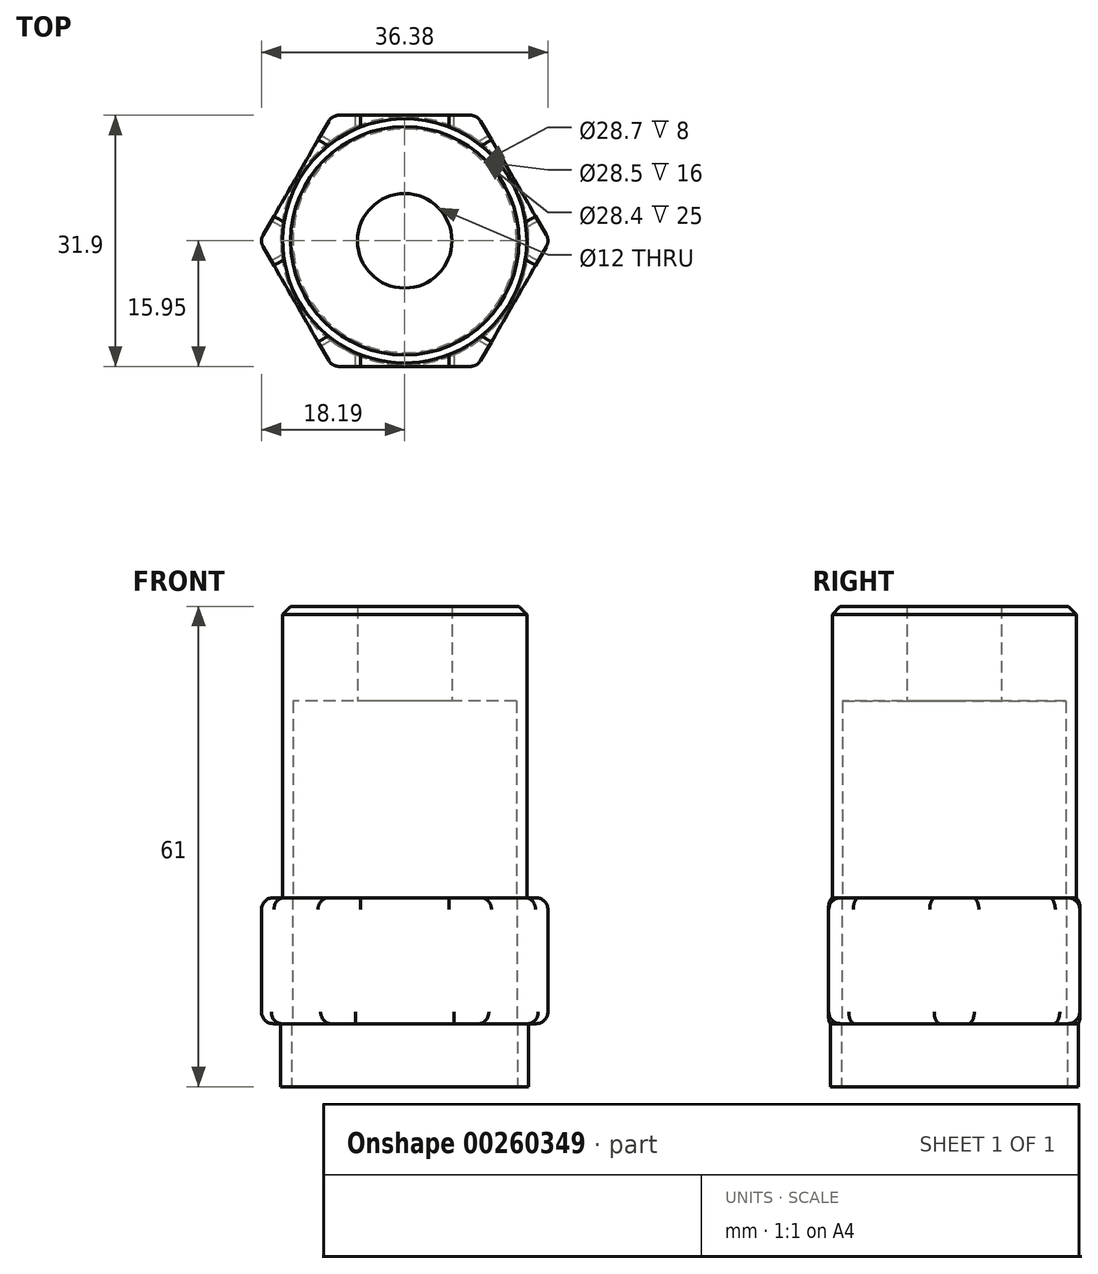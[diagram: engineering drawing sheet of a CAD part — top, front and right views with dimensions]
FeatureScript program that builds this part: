
annotation { "Feature Type Name" : "Feature", "Feature Type Description" : "" }
export const myFeature = defineFeature(function(context is Context, id is Id, definition is map)
    precondition{}
    {
        {
            var Q0;
            Q0=qCreatedBy(makeId("Top.planeOp"),FACE);
            var sketch = newSketch(context, id + "F0", { "sketchPlane" : qUnion([Q0])});
            skCircle(sketch, "E0", {"center": v(0, 0) * mm, "radius": 15.75 * mm});
            skCircle(sketch, "E1", {"center": v(0, 0) * mm, "radius": 14.35 * mm});
            skSolve(sketch);
        }
        {
            var Q0;
            Q0=qSketchRegion(id+"F0",true);
            extrude(context, id + "F1", {"entities" : qUnion([Q0]), "depth" : 8 * mm});
        }
        {
            var Q0;
            Q0=makeQuery(id+"F1.opExtrude","CAP_FACE",FACE,{"disambiguationData":[OSD([sQuery(id+"F0.wireOp",EDGE,"E0"),sQuery(id+"F0.wireOp",EDGE,"E1")])],"isStart":false});
            var sketch = newSketch(context, id + "F2", { "sketchPlane" : qUnion([Q0])});
            skCircle(sketch, "E2.cCircle", {"center": v(0, 0) * mm, "radius": 15.95 * mm, "construction": true});
            skLineSegment(sketch, "E2.0", {"start": v(-9.2, 15.95) * mm, "end": v(9.2, 15.95) * mm});
            skLineSegment(sketch, "E2.1", {"start": v(9.2, 15.95) * mm, "end": v(18.42, 0) * mm});
            skLineSegment(sketch, "E2.2", {"start": v(18.42, 0) * mm, "end": v(9.2, -15.95) * mm});
            skLineSegment(sketch, "E2.3", {"start": v(9.2, -15.95) * mm, "end": v(-9.2, -15.95) * mm});
            skLineSegment(sketch, "E2.4", {"start": v(-9.2, -15.95) * mm, "end": v(-18.42, 0) * mm});
            skLineSegment(sketch, "E2.5", {"start": v(-18.42, 0) * mm, "end": v(-9.2, 15.95) * mm});
            skPoint(sketch, "E2.0.midPoint", {"position": v(0, 15.95) * mm});
            skCircle(sketch, "E3", {"center": v(0, 0) * mm, "radius": 14.25 * mm});
            skSolve(sketch);
        }
        {
            var Q0;
            Q0=qSketchRegion(id+"F2",true);
            extrude(context, id + "F3", {"entities" : qUnion([Q0]), "operationType" : NewBodyOperationType.ADD, "depth" : 16 * mm});
        }
        {
            var Q0;
            Q0=makeQuery(id+"F3.opExtrude","CAP_FACE",FACE,{"disambiguationData":[OSD([sQuery(id+"F2.wireOp",EDGE,"E2.0"),sQuery(id+"F2.wireOp",EDGE,"E2.1"),sQuery(id+"F2.wireOp",EDGE,"E2.2"),sQuery(id+"F2.wireOp",EDGE,"E2.3"),sQuery(id+"F2.wireOp",EDGE,"E2.4"),sQuery(id+"F2.wireOp",EDGE,"E2.5"),sQuery(id+"F2.wireOp",EDGE,"E3")])],"isStart":false});
            var sketch = newSketch(context, id + "F4", { "sketchPlane" : qUnion([Q0])});
            skCircle(sketch, "E4", {"center": v(0, 0) * mm, "radius": 14.2 * mm});
            skCircle(sketch, "E5", {"center": v(0, 0) * mm, "radius": 15.5 * mm});
            skSolve(sketch);
        }
        {
            var Q0;
            Q0=qSketchRegion(id+"F4",true);
            extrude(context, id + "F5", {"entities" : qUnion([Q0]), "operationType" : NewBodyOperationType.ADD, "depth" : 25 * mm});
        }
        {
            var Q0;
            Q0=makeQuery(id+"F5.opExtrude","CAP_FACE",FACE,{"disambiguationData":[OSD([sQuery(id+"F4.wireOp",EDGE,"E4"),sQuery(id+"F4.wireOp",EDGE,"E5")])],"isStart":false});
            var sketch = newSketch(context, id + "F6", { "sketchPlane" : qUnion([Q0])});
            skCircle(sketch, "E6", {"center": v(0, 0) * mm, "radius": 15.5 * mm});
            skCircle(sketch, "E7", {"center": v(0, 0) * mm, "radius": 6 * mm});
            skSolve(sketch);
        }
        {
            var Q0;
            Q0=qSketchRegion(id+"F6",true);
            extrude(context, id + "F7", {"entities" : qUnion([Q0]), "operationType" : NewBodyOperationType.ADD, "depth" : 12 * mm});
        }
        {
            var Q0;
            Q0=makeQuery(id+"F3.opExtrude","SWEPT_EDGE",EDGE,{"disambiguationData":[OSD([sQuery(id+"F2.wireOp",EDGE,"E2.1"),sQuery(id+"F2.wireOp",EDGE,"E2.2")])]});
            var Q1;
            Q1=makeQuery(id+"F3.opExtrude","SWEPT_EDGE",EDGE,{"disambiguationData":[OSD([sQuery(id+"F2.wireOp",EDGE,"E2.2"),sQuery(id+"F2.wireOp",EDGE,"E2.3")])]});
            var Q2;
            Q2=makeQuery(id+"F3.opExtrude","SWEPT_EDGE",EDGE,{"disambiguationData":[OSD([sQuery(id+"F2.wireOp",EDGE,"E2.3"),sQuery(id+"F2.wireOp",EDGE,"E2.4")])]});
            var Q3;
            Q3=makeQuery(id+"F3.opExtrude","SWEPT_EDGE",EDGE,{"disambiguationData":[OSD([sQuery(id+"F2.wireOp",EDGE,"E2.0"),sQuery(id+"F2.wireOp",EDGE,"E2.1")])]});
            var Q4;
            Q4=makeQuery(id+"F3.opExtrude","SWEPT_EDGE",EDGE,{"disambiguationData":[OSD([sQuery(id+"F2.wireOp",EDGE,"E2.0"),sQuery(id+"F2.wireOp",EDGE,"E2.5")])]});
            var Q5;
            Q5=makeQuery(id+"F3.opExtrude","SWEPT_EDGE",EDGE,{"disambiguationData":[OSD([sQuery(id+"F2.wireOp",EDGE,"E2.4"),sQuery(id+"F2.wireOp",EDGE,"E2.5")])]});
            var Q6;
            Q6=makeQuery(id+"F3.opExtrude","CAP_EDGE",EDGE,{"disambiguationData":[OSD([sQuery(id+"F2.wireOp",EDGE,"E2.0")])],"isStart":false});
            var Q7;
            Q7=makeQuery(id+"F3.opExtrude","CAP_EDGE",EDGE,{"disambiguationData":[OSD([sQuery(id+"F2.wireOp",EDGE,"E2.1")])],"isStart":false});
            var Q8;
            Q8=makeQuery(id+"F3.opExtrude","CAP_EDGE",EDGE,{"disambiguationData":[OSD([sQuery(id+"F2.wireOp",EDGE,"E2.2")])],"isStart":false});
            var Q9;
            Q9=makeQuery(id+"F3.opExtrude","CAP_EDGE",EDGE,{"disambiguationData":[OSD([sQuery(id+"F2.wireOp",EDGE,"E2.3")])],"isStart":false});
            var Q10;
            Q10=makeQuery(id+"F3.opExtrude","CAP_EDGE",EDGE,{"disambiguationData":[OSD([sQuery(id+"F2.wireOp",EDGE,"E2.4")])],"isStart":false});
            var Q11;
            Q11=makeQuery(id+"F3.opExtrude","CAP_EDGE",EDGE,{"disambiguationData":[OSD([sQuery(id+"F2.wireOp",EDGE,"E2.5")])],"isStart":false});
            var Q12;
            Q12=makeQuery(id+"F3.opExtrude","CAP_EDGE",EDGE,{"disambiguationData":[OSD([sQuery(id+"F2.wireOp",EDGE,"E2.5")])],"isStart":true});
            var Q13;
            Q13=makeQuery(id+"F3.opExtrude","CAP_EDGE",EDGE,{"disambiguationData":[OSD([sQuery(id+"F2.wireOp",EDGE,"E2.0")])],"isStart":true});
            var Q14;
            Q14=makeQuery(id+"F3.opExtrude","CAP_EDGE",EDGE,{"disambiguationData":[OSD([sQuery(id+"F2.wireOp",EDGE,"E2.4")])],"isStart":true});
            var Q15;
            Q15=makeQuery(id+"F3.opExtrude","CAP_EDGE",EDGE,{"disambiguationData":[OSD([sQuery(id+"F2.wireOp",EDGE,"E2.3")])],"isStart":true});
            var Q16;
            Q16=makeQuery(id+"F3.opExtrude","CAP_EDGE",EDGE,{"disambiguationData":[OSD([sQuery(id+"F2.wireOp",EDGE,"E2.2")])],"isStart":true});
            var Q17;
            Q17=makeQuery(id+"F3.opExtrude","CAP_EDGE",EDGE,{"disambiguationData":[OSD([sQuery(id+"F2.wireOp",EDGE,"E2.1")])],"isStart":true});
            fillet(context, id + "F8", {"entities" : qUnion([Q0, Q1, Q2, Q3, Q4, Q5, Q6, Q7, Q8, Q9, Q10, Q11, Q12, Q13, Q14, Q15, Q16, Q17]), "radius" : 1.5 * mm, "tangentPropagation" : true, "allowEdgeOverflow" : false});
        }
        {
            var Q0;
            Q0=makeQuery(id+"F7.opExtrude","CAP_EDGE",EDGE,{"disambiguationData":[OSD([sQuery(id+"F6.wireOp",EDGE,"E6")])],"isStart":false});
            chamfer(context, id + "F9", {"entities" : qUnion([Q0]), "width" : 1 * mm, "tangentPropagation" : true});
        }
    });
